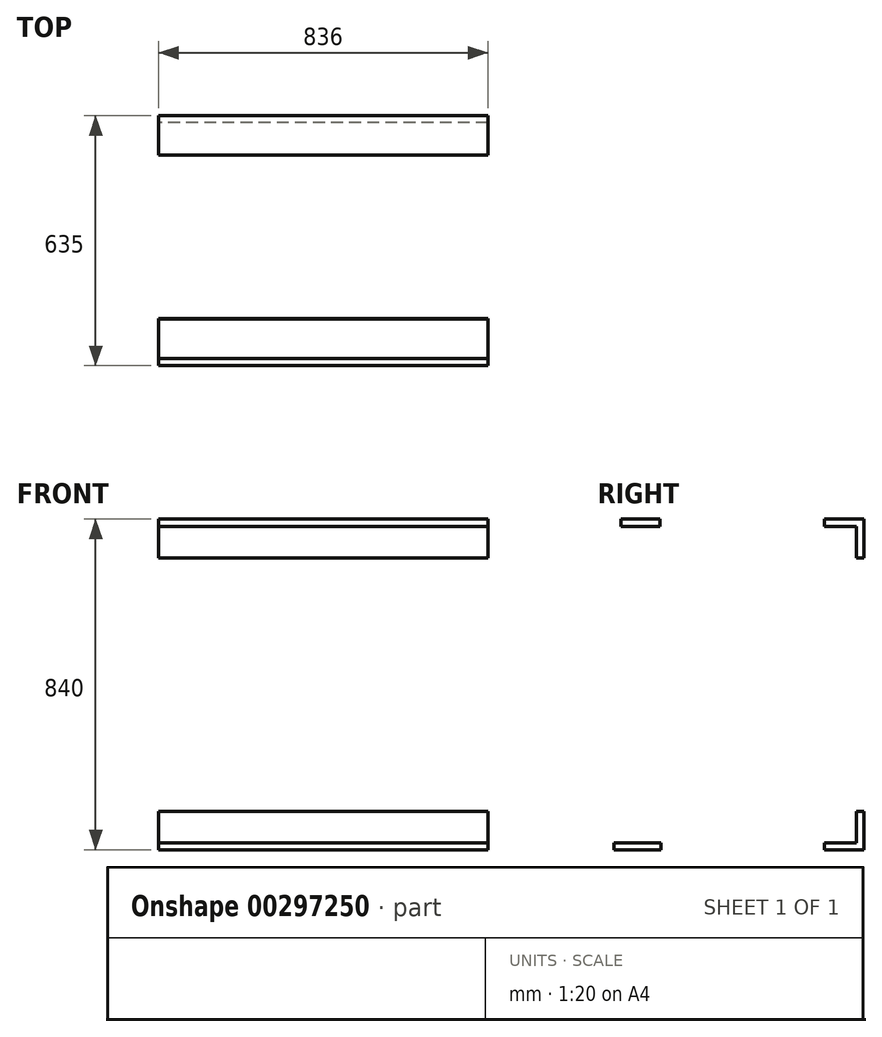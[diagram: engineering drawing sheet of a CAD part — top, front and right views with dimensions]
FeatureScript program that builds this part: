
annotation { "Feature Type Name" : "Feature", "Feature Type Description" : "" }
export const myFeature = defineFeature(function(context is Context, id is Id, definition is map)
    precondition{}
    {
        {
            var Q0;
            Q0=qCreatedBy(makeId("Right.planeOp"),FACE);
            var sketch = newSketch(context, id + "F0", { "sketchPlane" : qUnion([Q0])});
            skLineSegment(sketch, "E0.bottom", {"start": v(317.5, 420) * mm, "end": v(-317.5, 420) * mm, "construction": true});
            skLineSegment(sketch, "E0.top", {"start": v(317.5, -420) * mm, "end": v(-317.5, -420) * mm, "construction": true});
            skLineSegment(sketch, "E0.left", {"start": v(317.5, 420) * mm, "end": v(317.5, -420) * mm, "construction": true});
            skLineSegment(sketch, "E0.right", {"start": v(-317.5, 420) * mm, "end": v(-317.5, -420) * mm, "construction": true});
            skPoint(sketch, "E0.middle", {"position": v(0, 0) * mm});
            skLineSegment(sketch, "E1.bottom", {"start": v(317.5, 420) * mm, "end": v(217.5, 420) * mm});
            skLineSegment(sketch, "E1.top", {"start": v(317.5, 402) * mm, "end": v(217.5, 402) * mm});
            skLineSegment(sketch, "E1.left", {"start": v(317.5, 420) * mm, "end": v(317.5, 402) * mm});
            skLineSegment(sketch, "E1.right", {"start": v(217.5, 420) * mm, "end": v(217.5, 402) * mm});
            skLineSegment(sketch, "E2.bottom", {"start": v(317.5, 402) * mm, "end": v(299.5, 402) * mm});
            skLineSegment(sketch, "E2.top", {"start": v(317.5, 322) * mm, "end": v(299.5, 322) * mm});
            skLineSegment(sketch, "E2.left", {"start": v(317.5, 402) * mm, "end": v(317.5, 322) * mm});
            skLineSegment(sketch, "E2.right", {"start": v(299.5, 402) * mm, "end": v(299.5, 322) * mm});
            skLineSegment(sketch, "E3.bottom", {"start": v(-299.5, 420) * mm, "end": v(-199.5, 420) * mm});
            skLineSegment(sketch, "E3.top", {"start": v(-299.5, 402) * mm, "end": v(-199.5, 402) * mm});
            skLineSegment(sketch, "E3.left", {"start": v(-299.5, 420) * mm, "end": v(-299.5, 402) * mm});
            skLineSegment(sketch, "E3.right", {"start": v(-199.5, 420) * mm, "end": v(-199.5, 402) * mm});
            skLineSegment(sketch, "E4.bottom", {"start": v(-317.5, -420) * mm, "end": v(-197.5, -420) * mm});
            skLineSegment(sketch, "E4.top", {"start": v(-317.5, -402) * mm, "end": v(-197.5, -402) * mm});
            skLineSegment(sketch, "E4.left", {"start": v(-317.5, -420) * mm, "end": v(-317.5, -402) * mm});
            skLineSegment(sketch, "E4.right", {"start": v(-197.5, -420) * mm, "end": v(-197.5, -402) * mm});
            skLineSegment(sketch, "E5.bottom", {"start": v(317.5, -420) * mm, "end": v(217.5, -420) * mm});
            skLineSegment(sketch, "E5.top", {"start": v(317.5, -402) * mm, "end": v(217.5, -402) * mm});
            skLineSegment(sketch, "E5.left", {"start": v(317.5, -420) * mm, "end": v(317.5, -402) * mm});
            skLineSegment(sketch, "E5.right", {"start": v(217.5, -420) * mm, "end": v(217.5, -402) * mm});
            skLineSegment(sketch, "E6.bottom", {"start": v(317.5, -402) * mm, "end": v(299.5, -402) * mm});
            skLineSegment(sketch, "E6.top", {"start": v(317.5, -322) * mm, "end": v(299.5, -322) * mm});
            skLineSegment(sketch, "E6.left", {"start": v(317.5, -402) * mm, "end": v(317.5, -322) * mm});
            skLineSegment(sketch, "E6.right", {"start": v(299.5, -402) * mm, "end": v(299.5, -322) * mm});
            skSolve(sketch);
        }
        {
            var Q0;
            Q0 = qSketchRegion(id + "F0", true);
            extrude(context, id + "F1", {"entities" : qUnion([Q0]), "depth" : 836 * mm});
        }
    });
